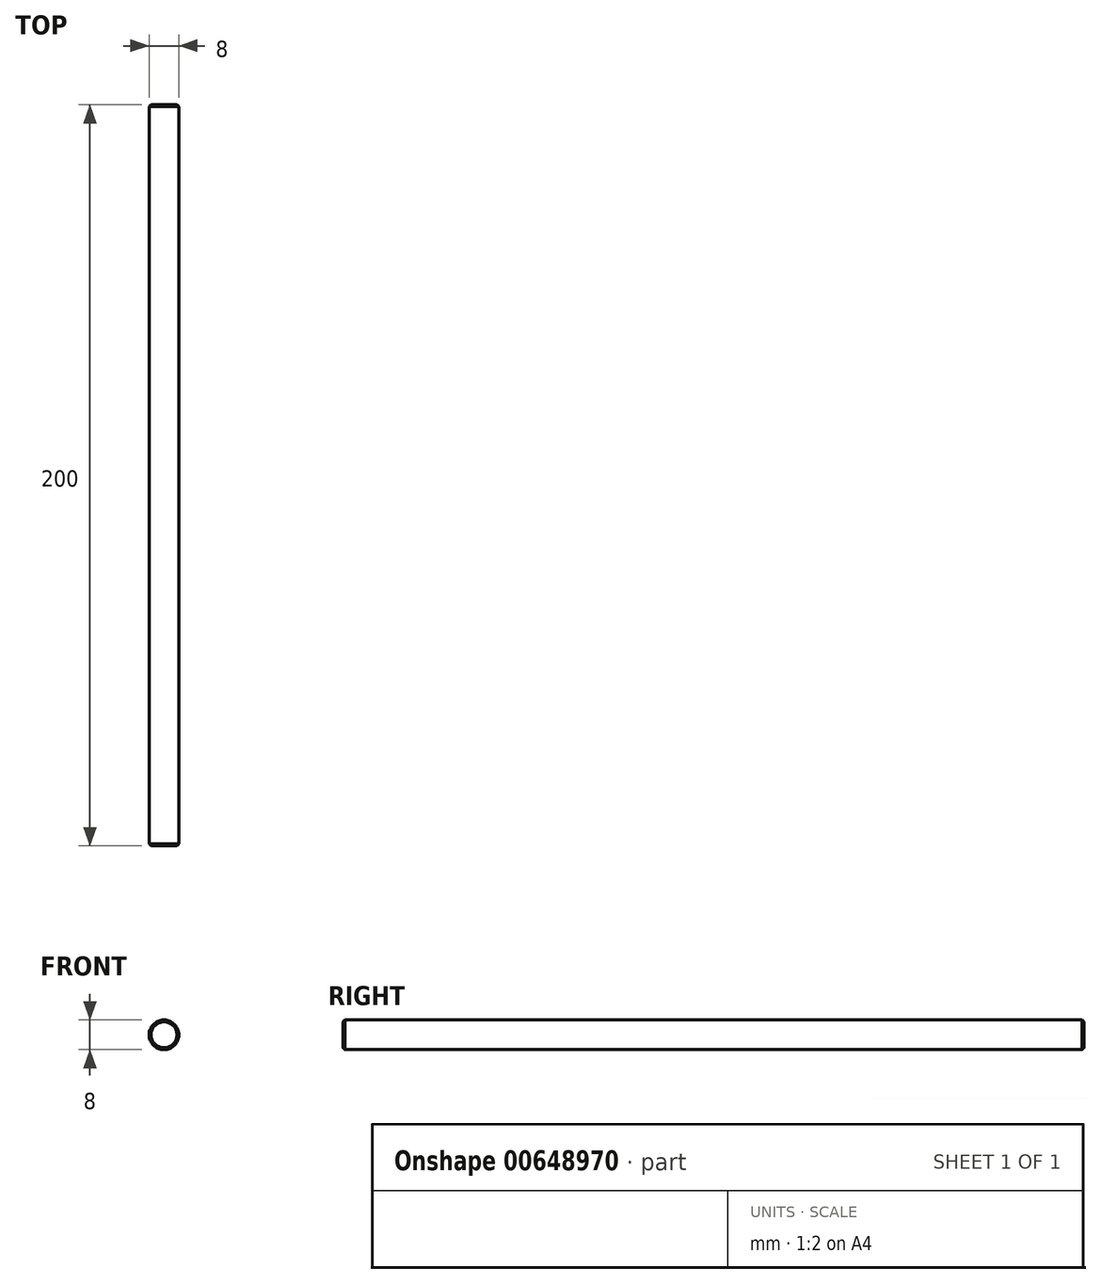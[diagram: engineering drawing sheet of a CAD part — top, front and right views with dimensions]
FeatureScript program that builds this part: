
annotation { "Feature Type Name" : "Feature", "Feature Type Description" : "" }
export const myFeature = defineFeature(function(context is Context, id is Id, definition is map)
    precondition{}
    {
        {
            var Q0;
            Q0=qCreatedBy(makeId("Front.planeOp"),FACE);
            var sketch = newSketch(context, id + "F0", { "sketchPlane" : qUnion([Q0])});
            skCircle(sketch, "E0", {"center": v(0, 0) * mm, "radius": 4 * mm});
            skSolve(sketch);
        }
        {
            var Q0;
            Q0 = qSketchRegion(id + "F0", true);
            extrude(context, id + "F1", {"entities" : qUnion([Q0]), "depth" : 200 * mm, "offsetDistance" : 25 * mm});
        }
        {
            var Q0;
            Q0=makeQuery(id+"F1.opExtrude","SWEPT_FACE",FACE,{"disambiguationData":[OSD([sQuery(id+"F0.wireOp",EDGE,"E0")])]});
            chamfer(context, id + "F2", {"entities" : qUnion([Q0]), "width" : 0.5 * mm, "tangentPropagation" : true});
        }
    });
